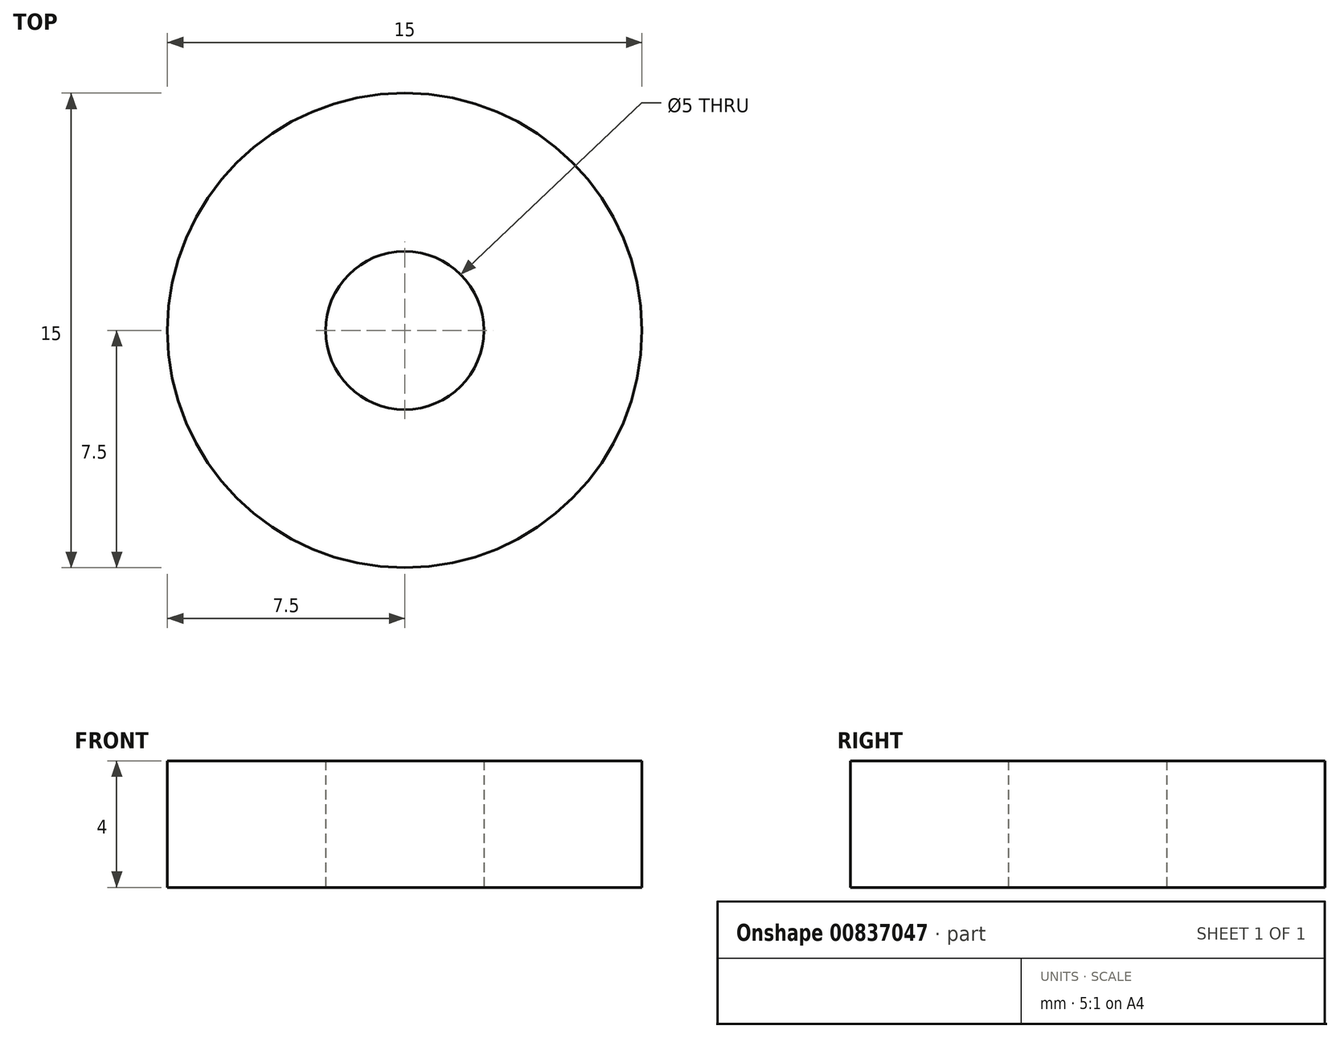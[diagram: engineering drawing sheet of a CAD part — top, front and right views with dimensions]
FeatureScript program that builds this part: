
annotation { "Feature Type Name" : "Feature", "Feature Type Description" : "" }
export const myFeature = defineFeature(function(context is Context, id is Id, definition is map)
    precondition{}
    {
        {
            var Q0;
            Q0=qCreatedBy(makeId("Top.planeOp"),FACE);
            var sketch = newSketch(context, id + "F0", { "sketchPlane" : qUnion([Q0])});
            skCircle(sketch, "E0", {"center": v(0, 0) * mm, "radius": 2.5 * mm});
            skCircle(sketch, "E1", {"center": v(0, 0) * mm, "radius": 7.5 * mm});
            skSolve(sketch);
        }
        {
            var Q0;
            Q0=makeQuery(id+"F0.imprint","IMPRINT",FACE,{"disambiguationData":[TD([[makeQuery(id+"F0.imprint","IMPRINT",EDGE,{"derivedFrom":sQuery(id+"F0.wireOp",EDGE,"E0")}),-1.0]])]});
            extrude(context, id + "F1", {"entities" : qUnion([Q0]), "depth" : 4 * mm, "offsetDistance" : 25 * mm});
        }
    });
